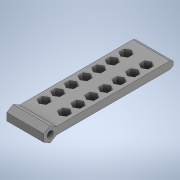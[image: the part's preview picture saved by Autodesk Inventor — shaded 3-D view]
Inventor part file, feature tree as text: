
AUTODESK INVENTOR PART (.ipt)
format: ipt  version: 2020 (Build 240168000, 168)  size: 294,400 bytes
history: native  units: in
note: dims shown in document units (in); Inventor stores cm internally (conversion verified against a paired STEP export)
features: sketch x4, extrude x3, plane x1, projected_geometry x1
ambient origin geometry x8: Origin, YZ Plane, XZ Plane, XY Plane, X Axis, Y Axis, Z Axis, Center Point
bodies: Solid1 (feature_tree)
feature tree (9):
  extrude  "Extrusion1"  Depth=2.7559in
  plane  "Work Plane1"
  extrude  "Extrusion2"  Depth=0.7874in
  extrude  "Extrusion3"  Depth=0.0787in
  sketch  "Sketch4"  dims[d6=0.7874in d7=0.0in d8=0.0787in d9=0.0787in d10=0.0787in d11=0.2273in d12=3.937in d14=0.2903in d15=0.3937in d17=0.3937in d19=3.937in d21=0.2903in d22=0.3937in d24=0.3937in d26=0.7874in d27=0.0in d28=2.4831in]
  sketch  "Sketch1"  dims[d0=0.1575in d1=2.7559in]
  sketch  "Sketch2"  dims[d2=0.1299in d3=0.7874in]
  sketch  "Sketch3"  dims[d4=0.0in d5=0.0787in]
  projected_geometry  "Projected Loop1"
